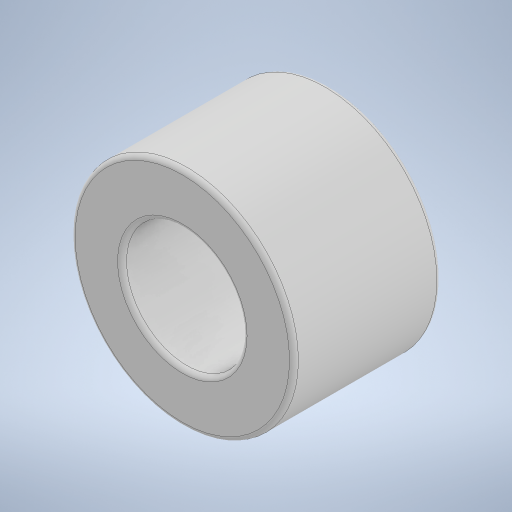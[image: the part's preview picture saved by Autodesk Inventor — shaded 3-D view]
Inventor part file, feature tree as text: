
AUTODESK INVENTOR PART (.ipt)
format: ipt  version: 2024 (Build 280153000, 153)  size: 250,368 bytes
history: native  units: in
note: dims shown in document units (in); Inventor stores cm internally (conversion verified against a paired STEP export)
features: extrude x1, fillet x1, direct_edit x1, sketch x1, other x1
ambient origin geometry x8: Origin, YZ Plane, XZ Plane, XY Plane, X Axis, Y Axis, Z Axis, Center Point
bodies: Solid1 (feature_tree)
feature tree (5):
  extrude  "Extrusion1"  Depth=0.3937in
  fillet  "Fillet1"  Radius=0.165in
  direct_edit  "Direct Edit1"
  sketch  "Sketch1"  dims[d0=0.25in d1=0.135in d2=0.165in d3=0.0in d4=0.005in d5=3.937in d6=0.3937in d7=0.3937in]
  other  "Scale1"
